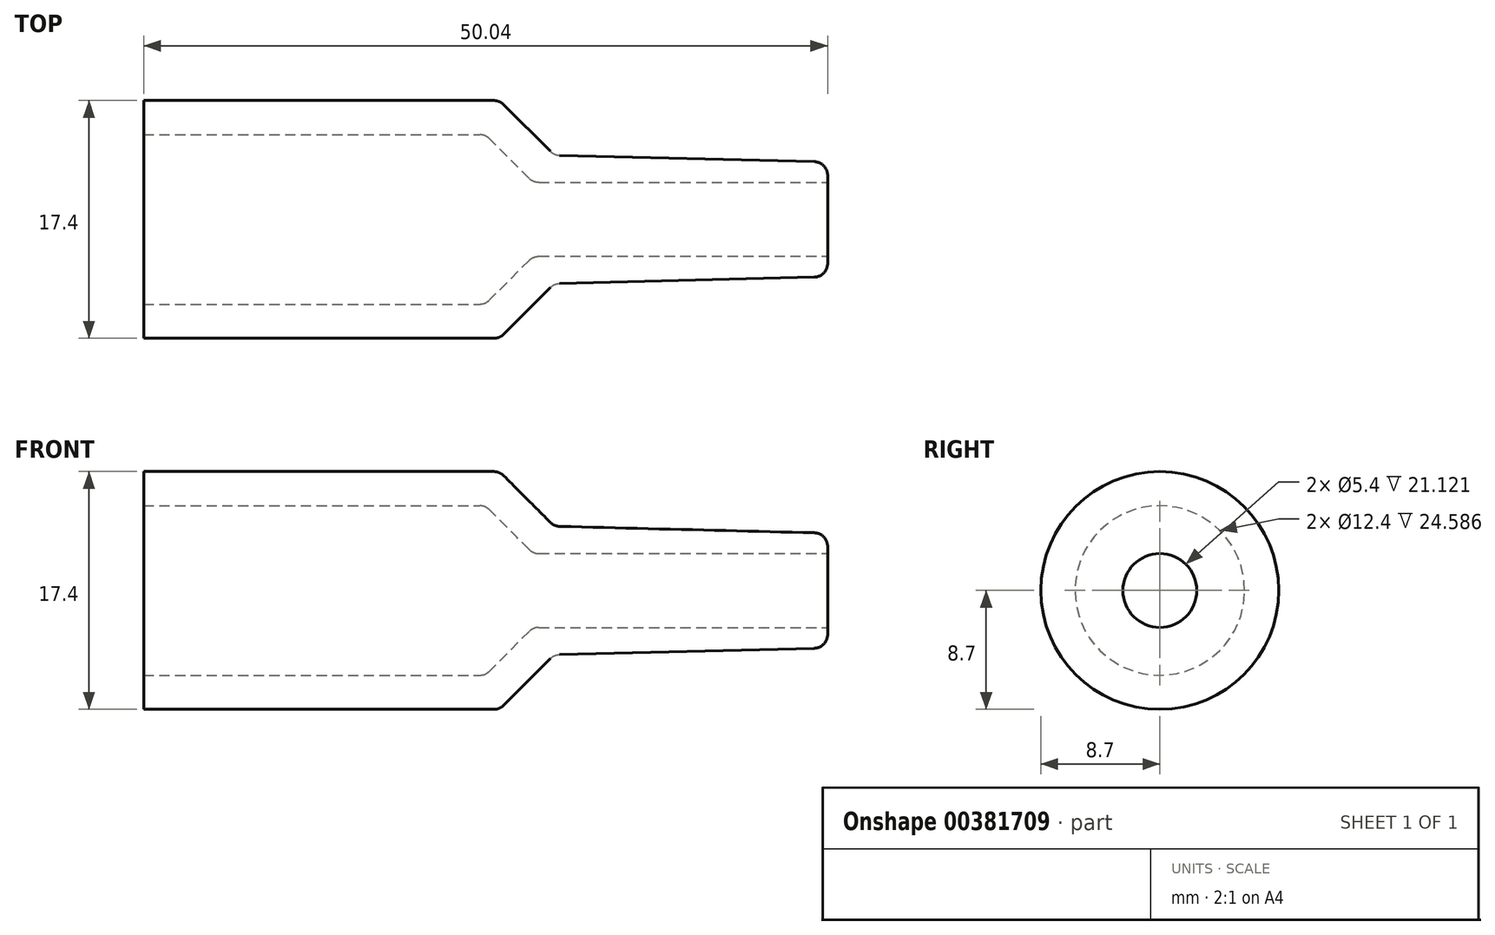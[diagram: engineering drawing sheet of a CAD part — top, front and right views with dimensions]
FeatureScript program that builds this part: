
annotation { "Feature Type Name" : "Feature", "Feature Type Description" : "" }
export const myFeature = defineFeature(function(context is Context, id is Id, definition is map)
    precondition{}
    {
        {
            var Q0;
            Q0=qCreatedBy(makeId("Front.planeOp"),FACE);
            var sketch = newSketch(context, id + "F0", { "sketchPlane" : qUnion([Q0])});
            skLineSegment(sketch, "E0", {"start": v(0, 0) * mm, "end": v(0, 8.7) * mm});
            skLineSegment(sketch, "E1", {"start": v(0, 8.7) * mm, "end": v(26.04, 8.7) * mm});
            skLineSegment(sketch, "E2", {"start": v(26.04, 8.7) * mm, "end": v(30.04, 4.7) * mm});
            skLineSegment(sketch, "E3", {"start": v(50.04, 4.2) * mm, "end": v(50.04, 0) * mm});
            skLineSegment(sketch, "E4", {"start": v(50.04, 0) * mm, "end": v(0, 0) * mm});
            skLineSegment(sketch, "E5", {"start": v(0, 6.2) * mm, "end": v(25, 6.2) * mm});
            skLineSegment(sketch, "E6", {"start": v(25, 6.2) * mm, "end": v(28.5, 2.7) * mm});
            skLineSegment(sketch, "E7", {"start": v(28.5, 2.7) * mm, "end": v(50.04, 2.7) * mm});
            skLineSegment(sketch, "E8", {"start": v(28.5, 2.7) * mm, "end": v(0, 2.7) * mm, "construction": true});
            skLineSegment(sketch, "E9", {"start": v(30.04, 4.7) * mm, "end": v(50.04, 4.2) * mm});
            skSolve(sketch);
        }
        {
            var Q0;
            {var subQ1=sQuery(id+"F0.wireOp",EDGE,"E1");Q0=makeQuery(id+"F0.imprint","IMPRINT",FACE,{"disambiguationData":[TD([[makeQuery(id+"F0.imprint","IMPRINT",EDGE,{"derivedFrom":subQ1}),-1.0]])]});}
            var Q1;
            Q1=sQuery(id+"F0.wireOp",EDGE,"E4");
            revolve(context, id + "F1", {"entities" : qUnion([Q0]), "axis" : qUnion([Q1]), "revolveType" : RevolveType.FULL});
        }
        {
            var Q0;
            Q0=makeQuery(id+"F1.opRevolve","SWEPT_EDGE",EDGE,{"disambiguationData":[OSD([sQuery(id+"F0.wireOp",EDGE,"E1"),sQuery(id+"F0.wireOp",EDGE,"E2")])]});
            var Q1;
            Q1=makeQuery(id+"F1.opRevolve","SWEPT_EDGE",EDGE,{"disambiguationData":[OSD([sQuery(id+"F0.wireOp",EDGE,"E2"),sQuery(id+"F0.wireOp",EDGE,"E9")])]});
            var Q2;
            Q2=makeQuery(id+"F1.opRevolve","SWEPT_EDGE",EDGE,{"disambiguationData":[OSD([sQuery(id+"F0.wireOp",EDGE,"E3"),sQuery(id+"F0.wireOp",EDGE,"E9")])]});
            var Q3;
            Q3=makeQuery(id+"F1.opRevolve","SWEPT_EDGE",EDGE,{"disambiguationData":[OSD([sQuery(id+"F0.wireOp",EDGE,"E5"),sQuery(id+"F0.wireOp",EDGE,"E6")])]});
            var Q4;
            Q4=makeQuery(id+"F1.opRevolve","SWEPT_EDGE",EDGE,{"disambiguationData":[OSD([sQuery(id+"F0.wireOp",EDGE,"E6"),sQuery(id+"F0.wireOp",EDGE,"E7")])]});
            fillet(context, id + "F2", {"entities" : qUnion([Q0, Q1, Q2, Q3, Q4]), "radius" : 1 * mm, "tangentPropagation" : true, "allowEdgeOverflow" : false});
        }
    });
